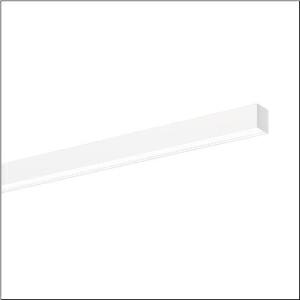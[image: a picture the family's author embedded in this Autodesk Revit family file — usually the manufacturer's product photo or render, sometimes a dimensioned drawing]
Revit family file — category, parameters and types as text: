
# Revit family: silica_r__21_51mx20da42wb_78eb
name_source: partatom
category: Lighting Fixtures
units: mm (PartAtom-declared; Revit-internal decimal feet)

## family parameters
Cut with Voids When Loaded = No
Host = Face
Light Source = No
Part Type = Normal
Room Calculation Point = No
Round Connector Dimension = Use Diameter
Shared = No

## types (1)
- --- (1 x LED, 2400 lm, 15.2 W, 4000K)
    Apparent Load = 15 VA
    CIE Flux Codes = 48 79 96 100 100
    Color Rendering = 80
    Color Temperature = 4000K
    Default Elevation = 1800 mm
    Description = Silica® 21, office luminaire, primary optical cover: cover, of PMMA, opal, light emission: direct distribution, primary light characteristic: symmetric, installation type: surface-mounted, LED, rated luminous flux: 2.400lm, luminous efficacy: 158lm/W, light colour: 840, colour temperature: 4000K, with terminal, 3+2-pole, max. 2.5mm², mains connection: 220..240V, AC, 50/60Hz, rated input power: 15.2W, luminaire housing, of aluminium, traffic white (RAL 9016), length: 1.204mm, width: 53mm, height: 53mm, protection rating (complete): IP20, insulation class (complete): insulation class I (protective earthing), certification: CE, permissible operating ambient temperature: 0..+35°C, standard: EN 50419, packaging unit: 1 piece
    Height = 0 mm  [stored 0 ft]
    Lamp = 1 x LED
    Lamp Light Flux = 2400 lm
    Lamp Power = 15.2 W
    Lamp count = 1
    Length = 1204 mm
    Luminous efficacy = 158 lm/W
    Manufacturer = Siteco
    ModVariant = No
    Model = 51MX20DA42WB
    Mounting Place = Ceiling
    Mounting Type = Recessed
    Number of Poles = 1
    OnlyDefault = Yes
    Power Factor = 1
    Product Name = Silica® 21
    Product group = office luminaire | ceiling recessed
    ProductGroupID = 401
    Protection Class = Protection class I
    Protection Degree = IP 20
    RLX_Detail_Level = 1
    RLX_Emergency_Light_Flux = 0 lm
    RLX_Emergency_Type = 0
    RLX_Emergency_Type_DB = No
    RlxData = <blob elided: 23877 chars, md5=644f769c>
    Socket = socket
    Standby Power = 0 W
    System Light Flux = 2400 lm
    System Power = 15 W
    Type Comments = factory setting: luminous flux: 100 % | dim-lin: 254 | 218 mA
    Type Image = l_1313601.jpg
    URL = http://relux.com
    VarID = @adj_066687
    Voltage = 0 V
    Weight = 0.00 kg
    Width = 53 mm

note: [stored X ft] marks values corroborated as IEEE doubles in the binary element streams (Revit-internal decimal feet)

## geometry (parser evidence)
native form markers: Blend x4, Sweep x9
no freeform markers — native parametric forms only
